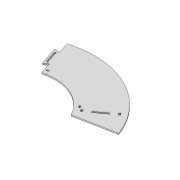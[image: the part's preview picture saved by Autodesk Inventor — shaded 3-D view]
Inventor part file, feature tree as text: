
AUTODESK INVENTOR PART (.ipt)
format: ipt  version: 2020 (Build 240168000, 168)  size: 312,832 bytes
history: native  units: mm
features: extrude x1, sketch x1
ambient origin geometry x8: Origin, YZ Plane, XZ Plane, XY Plane, X Axis, Y Axis, Z Axis, Center Point
bodies: Solid1 (feature_tree)
feature tree (2):
  extrude  "Extrusion1"  Depth=1.75mm
  sketch  "Sketch1"  dims[d0=504.787567mm d1=944.787567mm d2=50.0mm d4=360.0deg d6=7.5mm d7=7.5mm d9=68.5mm d10=7.5mm d11=7.5mm d12=3.5mm d13=3.5mm d17=50.0mm d19=360.0deg d21=4.363323mm d25=10.0mm d26=10.0mm d27=1.75mm d28=30.0mm d30=25.132741mm d32=271.25mm d33=7.5mm d34=13.5mm d36=1.75mm d40=20.0mm d44=7.0mm d45=0.0mm d46=0.0mm d47=8.0mm d48=1.75mm d50=50.0mm d52=50.0mm d54=30.0mm d62=50.0mm d64=50.0mm d66=30.0mm d67=1.75mm]
